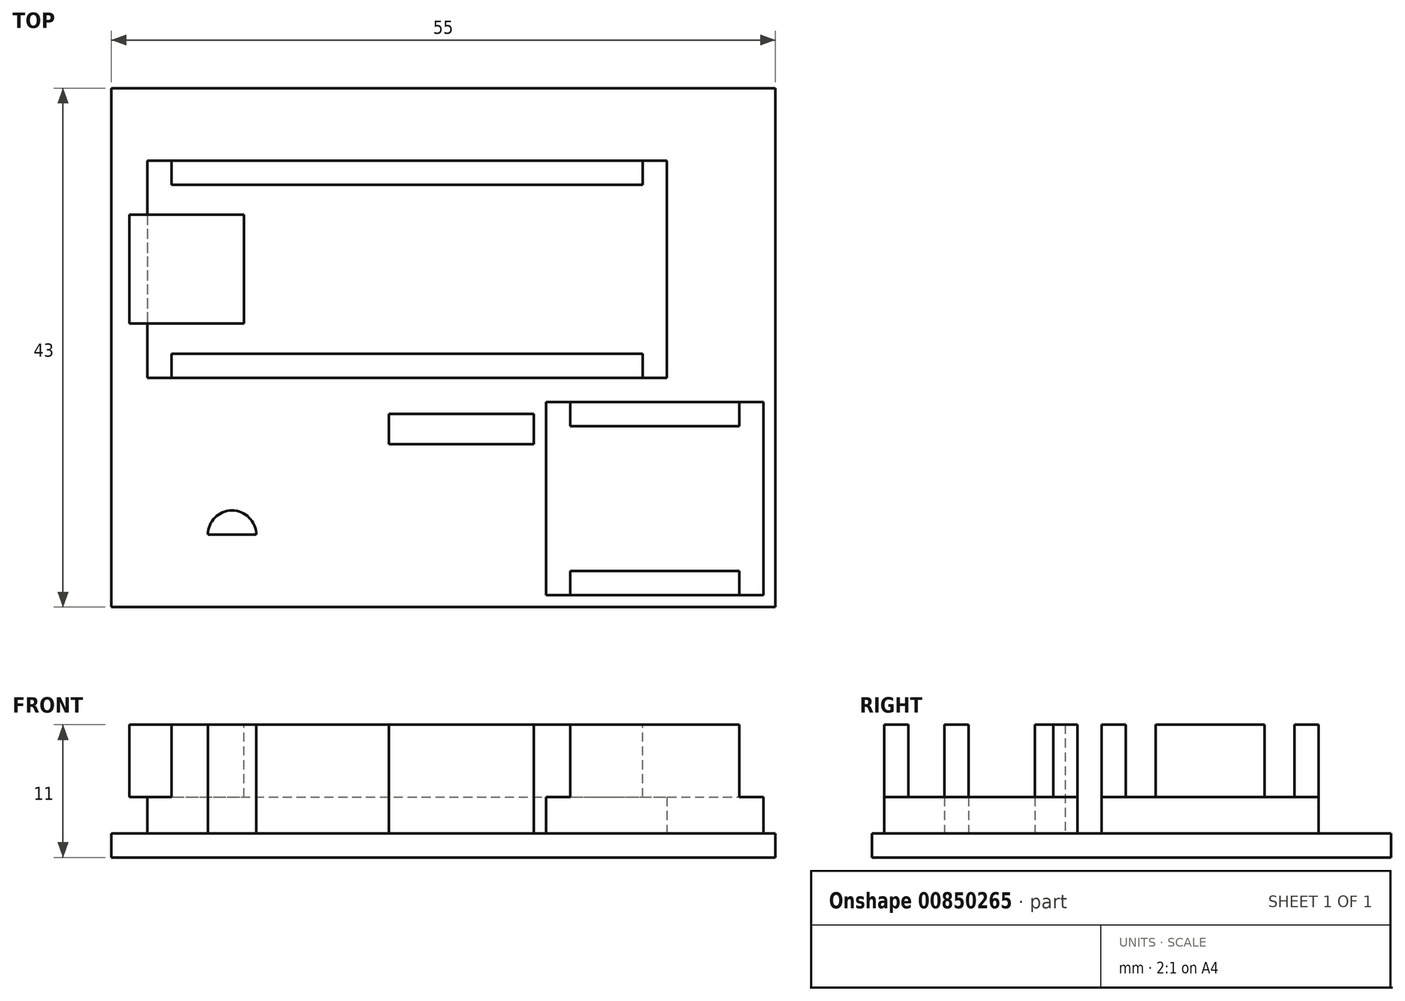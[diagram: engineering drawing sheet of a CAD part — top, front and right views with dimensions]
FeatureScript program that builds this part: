
annotation { "Feature Type Name" : "Feature", "Feature Type Description" : "" }
export const myFeature = defineFeature(function(context is Context, id is Id, definition is map)
    precondition{}
    {
        {
            var Q0;
            Q0=qCreatedBy(makeId("Top.planeOp"),FACE);
            var sketch = newSketch(context, id + "F0", { "sketchPlane" : qUnion([Q0])});
            skLineSegment(sketch, "E0.bottom", {"start": v(27.5, 21.5) * mm, "end": v(-27.5, 21.5) * mm});
            skLineSegment(sketch, "E0.top", {"start": v(27.5, -21.5) * mm, "end": v(-27.5, -21.5) * mm});
            skLineSegment(sketch, "E0.left", {"start": v(27.5, 21.5) * mm, "end": v(27.5, -21.5) * mm});
            skLineSegment(sketch, "E0.right", {"start": v(-27.5, 21.5) * mm, "end": v(-27.5, -21.5) * mm});
            skPoint(sketch, "E0.middle", {"position": v(0, 0) * mm});
            skSolve(sketch);
        }
        {
            var Q0;
            Q0=makeQuery(id+"F0.imprint","IMPRINT",FACE,{"disambiguationData":[TD([[makeQuery(id+"F0.imprint","IMPRINT",EDGE,{"derivedFrom":sQuery(id+"F0.wireOp",EDGE,"E0.bottom")}),1.0]])]});
            extrude(context, id + "F1", {"entities" : qUnion([Q0]), "depth" : 2 * mm, "offsetDistance" : 25.4 * mm});
        }
        {
            var Q0;
            Q0=makeQuery(id+"F1.opExtrude","CAP_FACE",FACE,{"disambiguationData":[OSD([sQuery(id+"F0.wireOp",EDGE,"E0.bottom"),sQuery(id+"F0.wireOp",EDGE,"E0.top"),sQuery(id+"F0.wireOp",EDGE,"E0.left"),sQuery(id+"F0.wireOp",EDGE,"E0.right")])],"isStart":false});
            var sketch = newSketch(context, id + "F2", { "sketchPlane" : qUnion([Q0])});
            skLineSegment(sketch, "E1.bottom", {"start": v(-24.5, 15.5) * mm, "end": v(18.5, 15.5) * mm});
            skLineSegment(sketch, "E1.top", {"start": v(-24.5, -2.5) * mm, "end": v(18.5, -2.5) * mm});
            skLineSegment(sketch, "E1.left", {"start": v(-24.5, 15.5) * mm, "end": v(-24.5, -2.5) * mm});
            skLineSegment(sketch, "E1.right", {"start": v(18.5, 15.5) * mm, "end": v(18.5, -2.5) * mm});
            skLineSegment(sketch, "E2.bottom", {"start": v(8.5, -4.5) * mm, "end": v(26.5, -4.5) * mm});
            skLineSegment(sketch, "E2.top", {"start": v(8.5, -20.5) * mm, "end": v(26.5, -20.5) * mm});
            skLineSegment(sketch, "E2.left", {"start": v(8.5, -4.5) * mm, "end": v(8.5, -20.5) * mm});
            skLineSegment(sketch, "E2.right", {"start": v(26.5, -4.5) * mm, "end": v(26.5, -20.5) * mm});
            skLineSegment(sketch, "E3.bottom", {"start": v(-4.5, -5.5) * mm, "end": v(7.5, -5.5) * mm});
            skLineSegment(sketch, "E3.top", {"start": v(-4.5, -8) * mm, "end": v(7.5, -8) * mm});
            skLineSegment(sketch, "E3.left", {"start": v(-4.5, -5.5) * mm, "end": v(-4.5, -8) * mm});
            skLineSegment(sketch, "E3.right", {"start": v(7.5, -5.5) * mm, "end": v(7.5, -8) * mm});
            skLineSegment(sketch, "E4", {"start": v(-19.5, -15.5) * mm, "end": v(-15.5, -15.5) * mm});
            skArc(sketch, "E5", {"start": v(-19.5, -15.5) * mm, "mid": v(-17.5, -13.5) * mm, "end": v(-15.5, -15.5) * mm});
            skSolve(sketch);
        }
        {
            var Q0;
            Q0=makeQuery(id+"F2.imprint","IMPRINT",FACE,{"disambiguationData":[TD([[makeQuery(id+"F2.imprint","IMPRINT",EDGE,{"derivedFrom":sQuery(id+"F2.wireOp",EDGE,"E1.bottom")}),-1.0]])]});
            var Q1;
            Q1=makeQuery(id+"F2.imprint","IMPRINT",FACE,{"disambiguationData":[TD([[makeQuery(id+"F2.imprint","IMPRINT",EDGE,{"derivedFrom":sQuery(id+"F2.wireOp",EDGE,"E3.bottom")}),-1.0]])]});
            var Q2;
            Q2=makeQuery(id+"F2.imprint","IMPRINT",FACE,{"disambiguationData":[TD([[makeQuery(id+"F2.imprint","IMPRINT",EDGE,{"derivedFrom":sQuery(id+"F2.wireOp",EDGE,"E2.bottom")}),-1.0]])]});
            var Q3;
            Q3=makeQuery(id+"F2.imprint","IMPRINT",FACE,{"disambiguationData":[TD([[makeQuery(id+"F2.imprint","IMPRINT",EDGE,{"derivedFrom":sQuery(id+"F2.wireOp",EDGE,"E4")}),1.0]])]});
            extrude(context, id + "F3", {"entities" : qUnion([Q0, Q1, Q2, Q3]), "operationType" : NewBodyOperationType.ADD, "depth" : 9 * mm, "offsetDistance" : 25.4 * mm});
        }
        {
            var Q0;
            Q0=makeQuery(id+"F3.opExtrude","CAP_FACE",FACE,{"disambiguationData":[OSD([sQuery(id+"F2.wireOp",EDGE,"E1.bottom"),sQuery(id+"F2.wireOp",EDGE,"E1.top"),sQuery(id+"F2.wireOp",EDGE,"E1.left"),sQuery(id+"F2.wireOp",EDGE,"E1.right")])],"isStart":false});
            var sketch = newSketch(context, id + "F4", { "sketchPlane" : qUnion([Q0])});
            skLineSegment(sketch, "E6.bottom", {"start": v(-22.5, 15.5) * mm, "end": v(16.5, 15.5) * mm});
            skLineSegment(sketch, "E6.top", {"start": v(-22.5, 13.5) * mm, "end": v(16.5, 13.5) * mm});
            skLineSegment(sketch, "E6.left", {"start": v(-22.5, 15.5) * mm, "end": v(-22.5, 13.5) * mm});
            skLineSegment(sketch, "E6.right", {"start": v(16.5, 15.5) * mm, "end": v(16.5, 13.5) * mm});
            skLineSegment(sketch, "E7.bottom", {"start": v(-22.5, -0.5) * mm, "end": v(16.5, -0.5) * mm});
            skLineSegment(sketch, "E7.top", {"start": v(-22.5, -2.5) * mm, "end": v(16.5, -2.5) * mm});
            skLineSegment(sketch, "E7.left", {"start": v(-22.5, -0.5) * mm, "end": v(-22.5, -2.5) * mm});
            skLineSegment(sketch, "E7.right", {"start": v(16.5, -0.5) * mm, "end": v(16.5, -2.5) * mm});
            skLineSegment(sketch, "E8.bottom", {"start": v(-24.5, 11) * mm, "end": v(-16.5, 11) * mm});
            skLineSegment(sketch, "E8.top", {"start": v(-24.5, 2) * mm, "end": v(-16.5, 2) * mm});
            skLineSegment(sketch, "E8.left", {"start": v(-24.5, 11) * mm, "end": v(-24.5, 2) * mm});
            skLineSegment(sketch, "E8.right", {"start": v(-16.5, 11) * mm, "end": v(-16.5, 2) * mm});
            skLineSegment(sketch, "E9.0.0", {"start": v(8.5, -4.5) * mm, "end": v(8.5, -20.5) * mm});
            skLineSegment(sketch, "E9.0.1", {"start": v(8.5, -20.5) * mm, "end": v(26.5, -20.5) * mm});
            skLineSegment(sketch, "E9.0.2", {"start": v(26.5, -20.5) * mm, "end": v(26.5, -4.5) * mm});
            skLineSegment(sketch, "E9.0.3", {"start": v(26.5, -4.5) * mm, "end": v(8.5, -4.5) * mm});
            skLineSegment(sketch, "E10.0.0", {"start": v(-24.5, 15.5) * mm, "end": v(-24.5, -2.5) * mm});
            skLineSegment(sketch, "E10.0.1", {"start": v(-24.5, -2.5) * mm, "end": v(18.5, -2.5) * mm});
            skLineSegment(sketch, "E10.0.2", {"start": v(18.5, -2.5) * mm, "end": v(18.5, 15.5) * mm});
            skLineSegment(sketch, "E10.0.3", {"start": v(18.5, 15.5) * mm, "end": v(-24.5, 15.5) * mm});
            skLineSegment(sketch, "E11.bottom", {"start": v(10.5, -4.5) * mm, "end": v(24.5, -4.5) * mm});
            skLineSegment(sketch, "E11.top", {"start": v(10.5, -6.5) * mm, "end": v(24.5, -6.5) * mm});
            skLineSegment(sketch, "E11.left", {"start": v(10.5, -4.5) * mm, "end": v(10.5, -6.5) * mm});
            skLineSegment(sketch, "E11.right", {"start": v(24.5, -4.5) * mm, "end": v(24.5, -6.5) * mm});
            skLineSegment(sketch, "E12.bottom", {"start": v(10.5, -18.5) * mm, "end": v(24.5, -18.5) * mm});
            skLineSegment(sketch, "E12.top", {"start": v(10.5, -20.5) * mm, "end": v(24.5, -20.5) * mm});
            skLineSegment(sketch, "E12.left", {"start": v(10.5, -18.5) * mm, "end": v(10.5, -20.5) * mm});
            skLineSegment(sketch, "E12.right", {"start": v(24.5, -18.5) * mm, "end": v(24.5, -20.5) * mm});
            skSolve(sketch);
        }
        {
            var Q0;
            Q0=makeQuery(id+"F4.imprint","IMPRINT",FACE,{"disambiguationData":[TD([[makeQuery(id+"F4.imprint","IMPRINT",EDGE,{"derivedFrom":sQuery(id+"F4.wireOp",EDGE,"E6.top")}),-1.0]])]});
            var Q1;
            {var subQ3=sQuery(id+"F4.wireOp",EDGE,"E9.0.0");Q1=makeQuery(id+"F4.imprint","IMPRINT",FACE,{"disambiguationData":[TD([[makeQuery(id+"F4.imprint","IMPRINT",EDGE,{"derivedFrom":subQ3}),1.0]])]});}
            extrude(context, id + "F5", {"entities" : qUnion([Q0, Q1]), "operationType" : NewBodyOperationType.REMOVE, "oppositeDirection" : true, "depth" : 6 * mm, "offsetDistance" : 25.4 * mm});
        }
        {
            var Q0;
            Q0=makeQuery(id+"F3.opExtrude","SWEPT_FACE",FACE,{"disambiguationData":[OSD([sQuery(id+"F2.wireOp",EDGE,"E1.left")])]});
            var sketch = newSketch(context, id + "F6", { "sketchPlane" : qUnion([Q0])});
            skLineSegment(sketch, "E13", {"start": v(-11, 5) * mm, "end": v(-2, 5) * mm});
            skLineSegment(sketch, "E14", {"start": v(-2, 5) * mm, "end": v(-2, 11) * mm});
            skLineSegment(sketch, "E15", {"start": v(-2, 11) * mm, "end": v(-11, 11) * mm});
            skLineSegment(sketch, "E16", {"start": v(-11, 11) * mm, "end": v(-11, 5) * mm});
            skSolve(sketch);
        }
        {
            var Q0;
            Q0=makeQuery(id+"F6.imprint","IMPRINT",FACE,{"disambiguationData":[TD([[makeQuery(id+"F6.imprint","IMPRINT",EDGE,{"derivedFrom":sQuery(id+"F6.wireOp",EDGE,"E13")}),1.0]])]});
            extrude(context, id + "F7", {"entities" : qUnion([Q0]), "operationType" : NewBodyOperationType.ADD, "depth" : 1.5 * mm, "offsetDistance" : 25.4 * mm});
        }
    });
